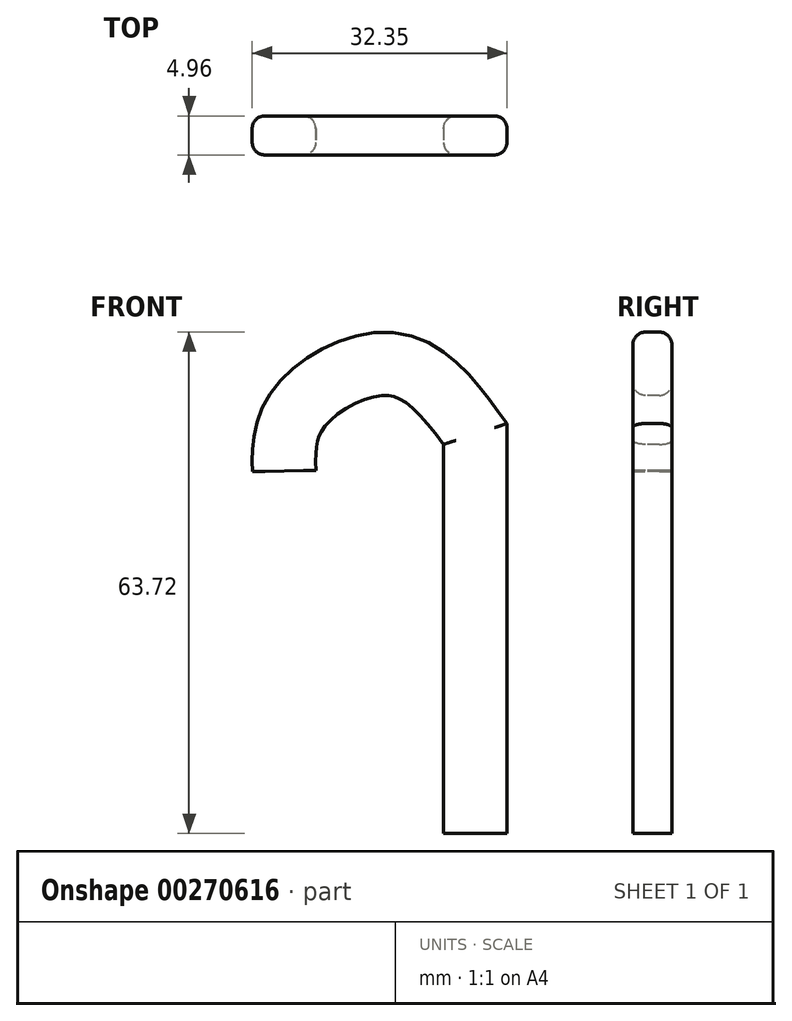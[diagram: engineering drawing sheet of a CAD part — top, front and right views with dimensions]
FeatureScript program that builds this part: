
annotation { "Feature Type Name" : "Feature", "Feature Type Description" : "" }
export const myFeature = defineFeature(function(context is Context, id is Id, definition is map)
    precondition{}
    {
        {
            var Q0;
            Q0=qCreatedBy(makeId("Top.planeOp"),FACE);
            var sketch = newSketch(context, id + "F0", { "sketchPlane" : qUnion([Q0])});
            skPoint(sketch, "E0.middle", {"position": v(0, 0) * mm});
            skLineSegment(sketch, "E1.bottom", {"start": v(2.44, 2.48) * mm, "end": v(-2.44, 2.48) * mm});
            skLineSegment(sketch, "E1.top", {"start": v(2.44, -2.48) * mm, "end": v(-2.44, -2.48) * mm});
            skLineSegment(sketch, "E1.left", {"start": v(4.02, 0.89) * mm, "end": v(4.02, -0.89) * mm});
            skLineSegment(sketch, "E1.right", {"start": v(-4.02, 0.89) * mm, "end": v(-4.02, -0.89) * mm});
            skPoint(sketch, "E2.visualSharp", {"position": v(4.02, -2.48) * mm});
            skArc(sketch, "E2.filletArc", {"start": v(2.44, -2.48) * mm, "mid": v(3.56, -2.01) * mm, "end": v(4.02, -0.89) * mm});
            skPoint(sketch, "E3.visualSharp", {"position": v(4.02, 2.48) * mm});
            skArc(sketch, "E3.filletArc", {"start": v(4.02, 0.89) * mm, "mid": v(3.56, 2.01) * mm, "end": v(2.44, 2.48) * mm});
            skPoint(sketch, "E4.visualSharp", {"position": v(-4.02, 2.48) * mm});
            skArc(sketch, "E4.filletArc", {"start": v(-2.44, 2.48) * mm, "mid": v(-3.56, 2.01) * mm, "end": v(-4.02, 0.89) * mm});
            skPoint(sketch, "E5.visualSharp", {"position": v(-4.02, -2.48) * mm});
            skArc(sketch, "E5.filletArc", {"start": v(-4.02, -0.89) * mm, "mid": v(-3.56, -2.01) * mm, "end": v(-2.44, -2.48) * mm});
            skSolve(sketch);
        }
        {
            var Q0;
            Q0=qCreatedBy(makeId("Front.planeOp"),FACE);
            var sketch = newSketch(context, id + "F1", { "sketchPlane" : qUnion([Q0])});
            skLineSegment(sketch, "E6", {"start": v(0, 0) * mm, "end": v(0, 50.78) * mm});
            skFitSpline(sketch, "E7", {"points": [v(0, 50.78) * mm, v(-10.47, 59.64) * mm, v(-22.6, 53.82) * mm, v(-24.29, 46.06) * mm], "startDerivative": vector(-25.37, 34.43) * mm, "endDerivative": vector(0.59, -28.47) * mm});
            skSolve(sketch);
        }
        {
            var Q0;
            Q0 = qSketchRegion(id + "F0", true);
            var Q1;
            Q1=sQuery(id+"F1.wireOp",EDGE,"E6");
            var Q2;
            Q2=sQuery(id+"F1.wireOp",EDGE,"E7");
            sweep(context, id + "F2", {"profiles" : qUnion([Q0]), "path" : qUnion([Q1, Q2])});
        }
    });
